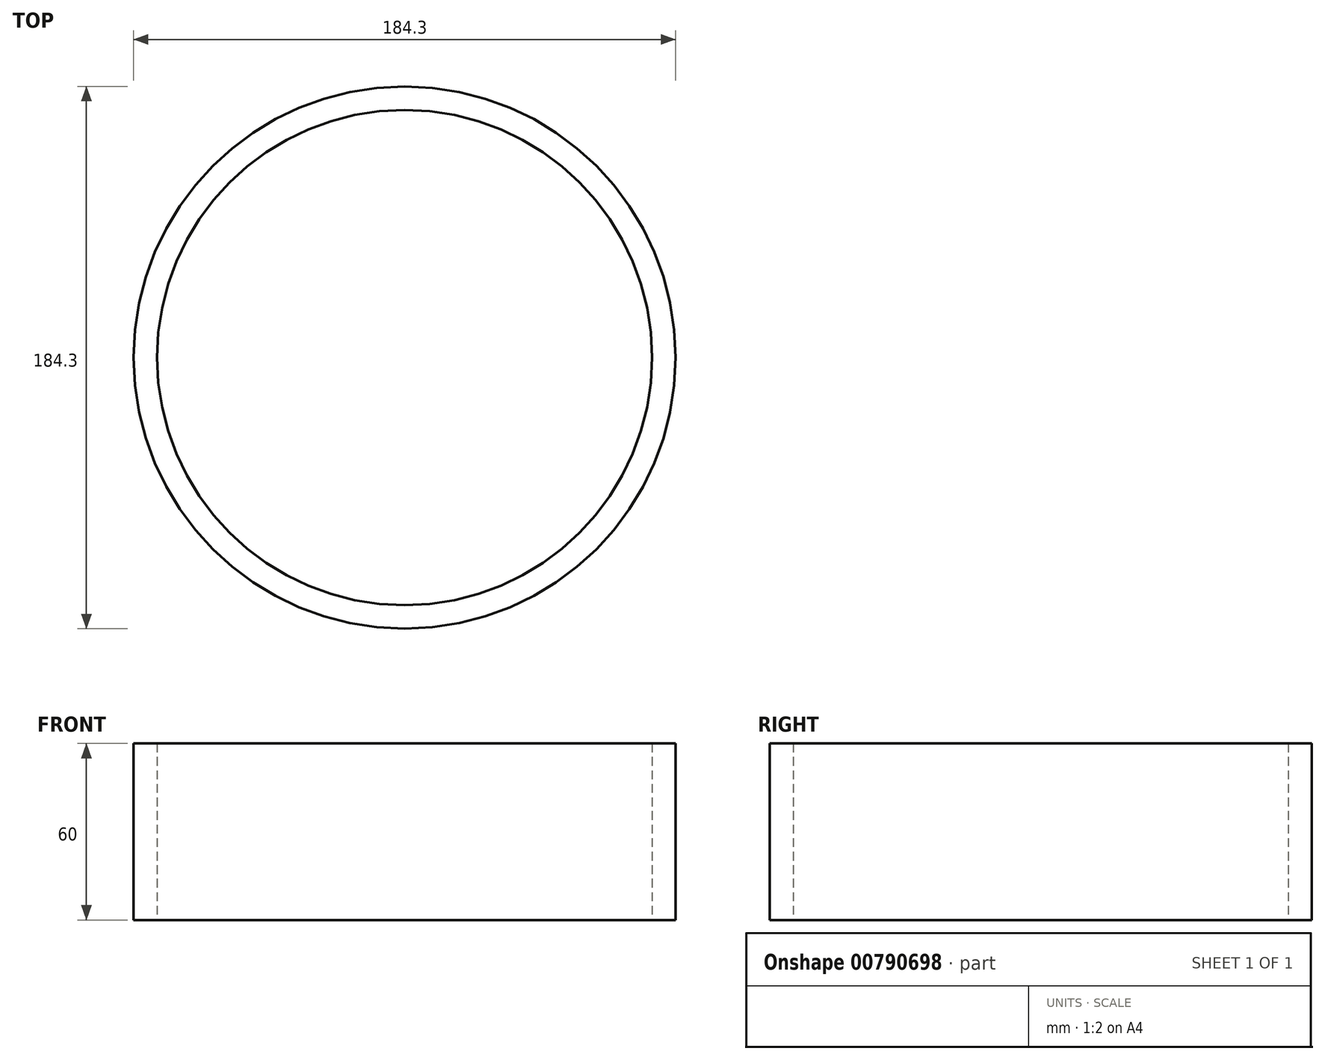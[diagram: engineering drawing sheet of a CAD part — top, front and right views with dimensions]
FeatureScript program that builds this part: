
annotation { "Feature Type Name" : "Feature", "Feature Type Description" : "" }
export const myFeature = defineFeature(function(context is Context, id is Id, definition is map)
    precondition{}
    {
        {
            var Q0;
            Q0=qCreatedBy(makeId("Top.planeOp"),FACE);
            var sketch = newSketch(context, id + "F0", { "sketchPlane" : qUnion([Q0])});
            skCircle(sketch, "E0", {"center": v(0, 0) * mm, "radius": 84.15 * mm});
            skCircle(sketch, "E1", {"center": v(0, 0) * mm, "radius": 92.15 * mm});
            skSolve(sketch);
        }
        {
            var Q0;
            Q0=makeQuery(id+"F0.imprint","IMPRINT",FACE,{"disambiguationData":[TD([[makeQuery(id+"F0.imprint","IMPRINT",EDGE,{"derivedFrom":sQuery(id+"F0.wireOp",EDGE,"E0")}),-1.0]])]});
            extrude(context, id + "F1", {"entities" : qUnion([Q0]), "depth" : 60 * mm, "offsetDistance" : 25 * mm});
        }
    });
